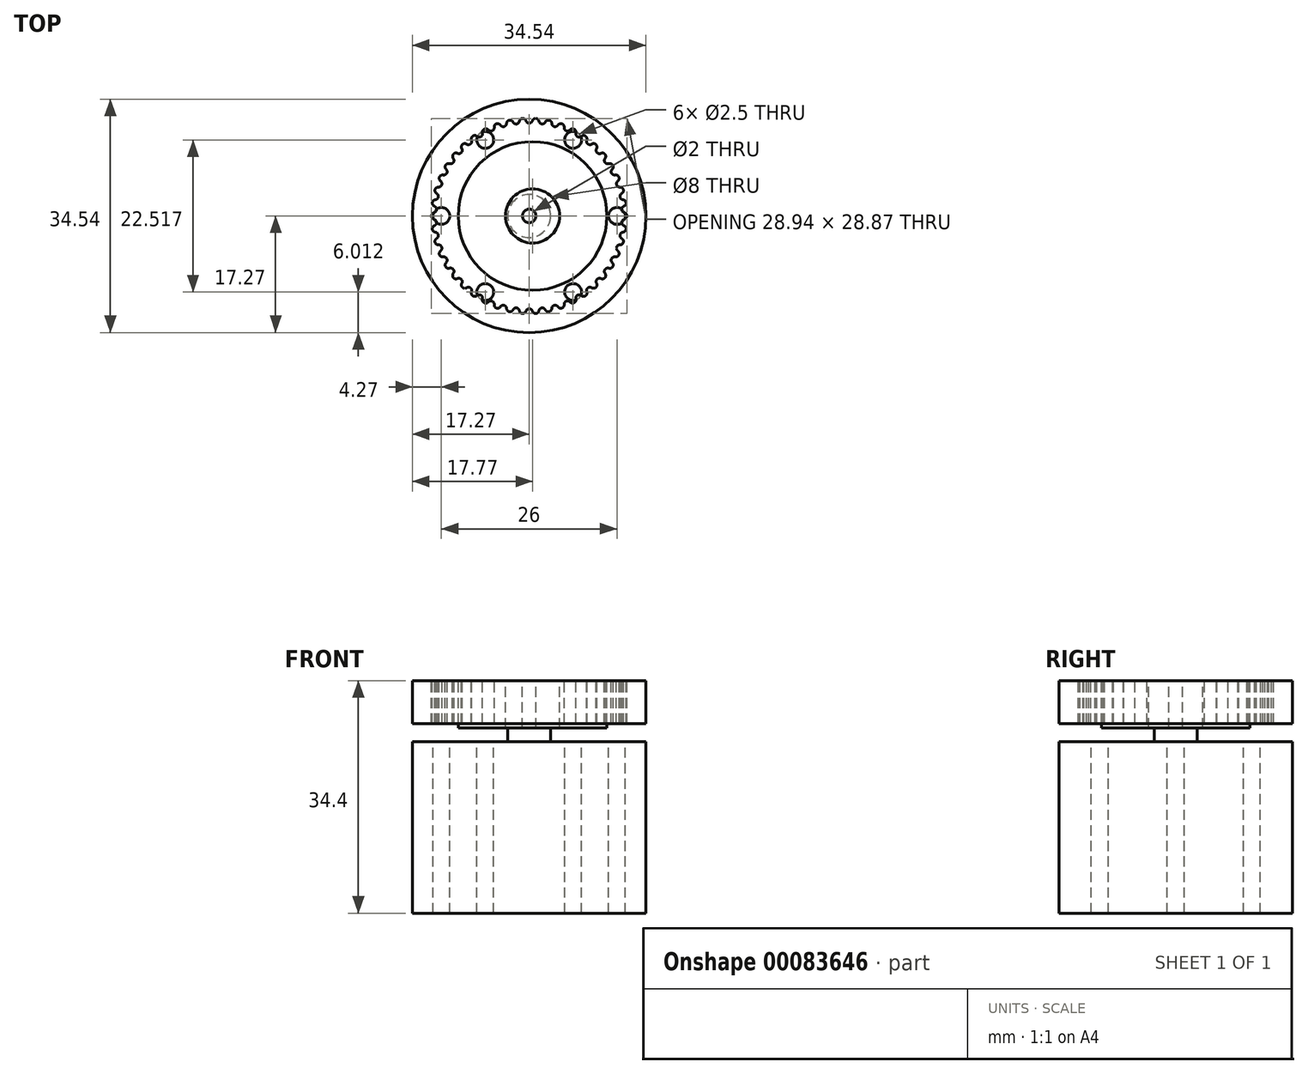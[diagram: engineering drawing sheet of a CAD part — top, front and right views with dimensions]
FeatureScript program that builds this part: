
annotation { "Feature Type Name" : "Feature", "Feature Type Description" : "" }
export const myFeature = defineFeature(function(context is Context, id is Id, definition is map)
    precondition{}
    {
        {
            var Q0;
            Q0=qCreatedBy(makeId("Top.planeOp"),FACE);
            var sketch = newSketch(context, id + "F0", { "sketchPlane" : qUnion([Q0])});
            skCircle(sketch, "E0", {"center": v(0, 0) * mm, "radius": 17.27 * mm});
            skCircle(sketch, "E1", {"center": v(13, 0) * mm, "radius": 1.25 * mm});
            skCircle(sketch, "E2.1.0", {"center": v(6.5, 11.26) * mm, "radius": 1.25 * mm});
            skCircle(sketch, "E2.2.0", {"center": v(-6.5, 11.26) * mm, "radius": 1.25 * mm});
            skCircle(sketch, "E2.3.0", {"center": v(-13, 0) * mm, "radius": 1.25 * mm});
            skCircle(sketch, "E2.4.0", {"center": v(-6.5, -11.26) * mm, "radius": 1.25 * mm});
            skCircle(sketch, "E2.5.0", {"center": v(6.5, -11.26) * mm, "radius": 1.25 * mm});
            skCircle(sketch, "E3", {"center": v(0, 0) * mm, "radius": 1 * mm});
            skCircle(sketch, "E4", {"center": v(0, 0) * mm, "radius": 3.18 * mm});
            skSolve(sketch);
        }
        {
            var Q0;
            Q0 = qSketchRegion(id + "F0", true);
            var Q1;
            Q1=makeQuery(id+"F0.imprint","IMPRINT",FACE,{"disambiguationData":[TD([[makeQuery(id+"F0.imprint","IMPRINT",EDGE,{"derivedFrom":sQuery(id+"F0.wireOp",EDGE,"E3")}),1.0]])]});
            var Q2;
            Q2=makeQuery(id+"F0.imprint","IMPRINT",FACE,{"disambiguationData":[TD([[makeQuery(id+"F0.imprint","IMPRINT",EDGE,{"derivedFrom":sQuery(id+"F0.wireOp",EDGE,"E3")}),-1.0]])]});
            extrude(context, id + "F1", {"entities" : qUnion([Q0, Q1, Q2]), "oppositeDirection" : true, "depth" : 25.4 * mm});
        }
        {
            var Q0;
            Q0=makeQuery(id+"F0.imprint","IMPRINT",FACE,{"disambiguationData":[TD([[makeQuery(id+"F0.imprint","IMPRINT",EDGE,{"derivedFrom":sQuery(id+"F0.wireOp",EDGE,"E3")}),1.0]])]});
            extrude(context, id + "F2", {"entities" : qUnion([Q0]), "operationType" : NewBodyOperationType.ADD, "depth" : 9 * mm});
        }
        {
            var Q0;
            Q0=makeQuery(id+"F0.imprint","IMPRINT",FACE,{"disambiguationData":[TD([[makeQuery(id+"F0.imprint","IMPRINT",EDGE,{"derivedFrom":sQuery(id+"F0.wireOp",EDGE,"E3")}),-1.0]])]});
            extrude(context, id + "F3", {"entities" : qUnion([Q0]), "operationType" : NewBodyOperationType.ADD, "depth" : 2 * mm});
        }
        {
            var Q0;
            Q0=makeQuery(id+"F1.opExtrude","CAP_FACE",FACE,{"disambiguationData":[OSD([sQuery(id+"F0.wireOp",EDGE,"E0"),sQuery(id+"F0.wireOp",EDGE,"E1"),sQuery(id+"F0.wireOp",EDGE,"E2.1.0"),sQuery(id+"F0.wireOp",EDGE,"E2.2.0"),sQuery(id+"F0.wireOp",EDGE,"E2.3.0"),sQuery(id+"F0.wireOp",EDGE,"E2.4.0"),sQuery(id+"F0.wireOp",EDGE,"E2.5.0")])],"isStart":true});
            var sketch = newSketch(context, id + "F4", { "sketchPlane" : qUnion([Q0])});
            skCircle(sketch, "E5.0.0", {"center": v(0, 0) * mm, "radius": 17.27 * mm});
            skCircle(sketch, "E6", {"center": v(0, 0) * mm, "radius": 16 * mm});
            skSolve(sketch);
        }
        {
            var Q0;
            Q0=makeQuery(id+"F2.opExtrude","CAP_FACE",FACE,{"disambiguationData":[OSD([sQuery(id+"F0.wireOp",EDGE,"E3")])],"isStart":false});
            var sketch = newSketch(context, id + "F5", { "sketchPlane" : qUnion([Q0])});
            skCircle(sketch, "E7", {"center": v(0.5, 0) * mm, "radius": 4 * mm});
            skCircle(sketch, "E8", {"center": v(0.5, 0) * mm, "radius": 11 * mm});
            skCircle(sketch, "E9.0", {"center": v(0, 0) * mm, "radius": 1 * mm});
            skArc(sketch, "E10", {"start": v(-14.09, 0.49) * mm, "mid": v(-14.47, 0) * mm, "end": v(-14.09, -0.49) * mm});
            skCircle(sketch, "E11", {"center": v(0, 0) * mm, "radius": 13.97 * mm, "construction": true});
            skArc(sketch, "E12", {"start": v(-14.09, 0.49) * mm, "mid": v(-13.72, 0.87) * mm, "end": v(-13.9, 1.37) * mm});
            skArc(sketch, "E13.MirrorC", {"start": v(-14.09, -0.49) * mm, "mid": v(-14.02, -0.5) * mm, "end": v(-13.96, -0.54) * mm});
            skLineSegment(sketch, "E14", {"start": v(-14.2, 0.97) * mm, "end": v(0, 0) * mm, "construction": true});
            skArc(sketch, "E15.1.0", {"start": v(-14.02, -1.44) * mm, "mid": v(-14.34, -1.97) * mm, "end": v(-13.9, -2.4) * mm});
            skArc(sketch, "E15.1.1", {"start": v(-13.9, -2.4) * mm, "mid": v(-13.82, -2.41) * mm, "end": v(-13.76, -2.43) * mm});
            skArc(sketch, "E15.1.2", {"start": v(-14.02, -1.44) * mm, "mid": v(-13.7, -1) * mm, "end": v(-13.96, -0.54) * mm});
            skArc(sketch, "E15.2.0", {"start": v(-13.7, -3.33) * mm, "mid": v(-13.93, -3.9) * mm, "end": v(-13.43, -4.27) * mm});
            skArc(sketch, "E15.2.1", {"start": v(-13.43, -4.27) * mm, "mid": v(-13.37, -4.27) * mm, "end": v(-13.3, -4.28) * mm});
            skArc(sketch, "E15.2.2", {"start": v(-13.7, -3.33) * mm, "mid": v(-13.44, -2.86) * mm, "end": v(-13.76, -2.43) * mm});
            skArc(sketch, "E15.3.0", {"start": v(-13.12, -5.17) * mm, "mid": v(-13.27, -5.76) * mm, "end": v(-12.73, -6.06) * mm});
            skArc(sketch, "E15.3.1", {"start": v(-12.73, -6.06) * mm, "mid": v(-12.66, -6.05) * mm, "end": v(-12.6, -6.05) * mm});
            skArc(sketch, "E15.3.2", {"start": v(-13.12, -5.17) * mm, "mid": v(-12.93, -4.67) * mm, "end": v(-13.3, -4.28) * mm});
            skArc(sketch, "E15.4.0", {"start": v(-12.29, -6.9) * mm, "mid": v(-12.36, -7.52) * mm, "end": v(-11.78, -7.74) * mm});
            skArc(sketch, "E15.4.1", {"start": v(-11.78, -7.74) * mm, "mid": v(-11.72, -7.72) * mm, "end": v(-11.65, -7.71) * mm});
            skArc(sketch, "E15.4.2", {"start": v(-12.29, -6.9) * mm, "mid": v(-12.17, -6.38) * mm, "end": v(-12.6, -6.05) * mm});
            skArc(sketch, "E15.5.0", {"start": v(-11.23, -8.51) * mm, "mid": v(-11.22, -9.13) * mm, "end": v(-10.62, -9.27) * mm});
            skArc(sketch, "E15.5.1", {"start": v(-10.62, -9.27) * mm, "mid": v(-10.56, -9.24) * mm, "end": v(-10.5, -9.23) * mm});
            skArc(sketch, "E15.5.2", {"start": v(-11.23, -8.51) * mm, "mid": v(-11.19, -7.98) * mm, "end": v(-11.65, -7.71) * mm});
            skArc(sketch, "E15.6.0", {"start": v(-9.97, -9.96) * mm, "mid": v(-9.88, -10.58) * mm, "end": v(-9.26, -10.63) * mm});
            skArc(sketch, "E15.6.1", {"start": v(-9.26, -10.63) * mm, "mid": v(-9.2, -10.6) * mm, "end": v(-9.14, -10.57) * mm});
            skArc(sketch, "E15.6.2", {"start": v(-9.97, -9.96) * mm, "mid": v(-10, -9.43) * mm, "end": v(-10.5, -9.23) * mm});
            skArc(sketch, "E15.7.0", {"start": v(-8.52, -11.23) * mm, "mid": v(-8.34, -11.82) * mm, "end": v(-7.73, -11.79) * mm});
            skArc(sketch, "E15.7.1", {"start": v(-7.73, -11.79) * mm, "mid": v(-7.67, -11.75) * mm, "end": v(-7.61, -11.71) * mm});
            skArc(sketch, "E15.7.2", {"start": v(-8.52, -11.23) * mm, "mid": v(-8.62, -10.7) * mm, "end": v(-9.14, -10.57) * mm});
            skArc(sketch, "E15.8.0", {"start": v(-6.91, -12.29) * mm, "mid": v(-6.66, -12.85) * mm, "end": v(-6.05, -12.73) * mm});
            skArc(sketch, "E15.8.1", {"start": v(-6.05, -12.73) * mm, "mid": v(-6, -12.68) * mm, "end": v(-5.95, -12.64) * mm});
            skArc(sketch, "E15.8.2", {"start": v(-6.91, -12.29) * mm, "mid": v(-7.08, -11.78) * mm, "end": v(-7.61, -11.71) * mm});
            skArc(sketch, "E15.9.0", {"start": v(-5.18, -13.11) * mm, "mid": v(-4.85, -13.63) * mm, "end": v(-4.26, -13.44) * mm});
            skArc(sketch, "E15.9.1", {"start": v(-4.26, -13.44) * mm, "mid": v(-4.22, -13.38) * mm, "end": v(-4.17, -13.33) * mm});
            skArc(sketch, "E15.9.2", {"start": v(-5.18, -13.11) * mm, "mid": v(-5.41, -12.63) * mm, "end": v(-5.95, -12.64) * mm});
            skArc(sketch, "E15.10.0", {"start": v(-3.34, -13.7) * mm, "mid": v(-2.94, -14.17) * mm, "end": v(-2.4, -13.9) * mm});
            skArc(sketch, "E15.10.1", {"start": v(-2.4, -13.9) * mm, "mid": v(-2.36, -13.83) * mm, "end": v(-2.31, -13.78) * mm});
            skArc(sketch, "E15.10.2", {"start": v(-3.34, -13.7) * mm, "mid": v(-3.64, -13.25) * mm, "end": v(-4.17, -13.33) * mm});
            skArc(sketch, "E15.11.0", {"start": v(-1.45, -14.02) * mm, "mid": v(-0.99, -14.44) * mm, "end": v(-0.48, -14.09) * mm});
            skArc(sketch, "E15.11.1", {"start": v(-0.48, -14.09) * mm, "mid": v(-0.45, -14.02) * mm, "end": v(-0.42, -13.96) * mm});
            skArc(sketch, "E15.11.2", {"start": v(-1.45, -14.02) * mm, "mid": v(-1.8, -13.63) * mm, "end": v(-2.31, -13.78) * mm});
            skArc(sketch, "E15.12.0", {"start": v(0.48, -14.09) * mm, "mid": v(0.99, -14.44) * mm, "end": v(1.45, -14.02) * mm});
            skArc(sketch, "E15.12.1", {"start": v(1.45, -14.02) * mm, "mid": v(1.46, -13.95) * mm, "end": v(1.49, -13.9) * mm});
            skArc(sketch, "E15.12.2", {"start": v(0.48, -14.09) * mm, "mid": v(0.07, -13.74) * mm, "end": v(-0.42, -13.96) * mm});
            skArc(sketch, "E15.13.0", {"start": v(2.4, -13.9) * mm, "mid": v(2.94, -14.17) * mm, "end": v(3.34, -13.7) * mm});
            skArc(sketch, "E15.13.1", {"start": v(3.34, -13.7) * mm, "mid": v(3.35, -13.63) * mm, "end": v(3.37, -13.56) * mm});
            skArc(sketch, "E15.13.2", {"start": v(2.4, -13.9) * mm, "mid": v(1.94, -13.6) * mm, "end": v(1.49, -13.9) * mm});
            skArc(sketch, "E15.14.0", {"start": v(4.26, -13.44) * mm, "mid": v(4.85, -13.63) * mm, "end": v(5.18, -13.11) * mm});
            skArc(sketch, "E15.14.1", {"start": v(5.18, -13.11) * mm, "mid": v(5.17, -13.04) * mm, "end": v(5.18, -12.97) * mm});
            skArc(sketch, "E15.14.2", {"start": v(4.26, -13.44) * mm, "mid": v(3.77, -13.22) * mm, "end": v(3.37, -13.56) * mm});
            skArc(sketch, "E15.15.0", {"start": v(6.05, -12.73) * mm, "mid": v(6.66, -12.85) * mm, "end": v(6.91, -12.29) * mm});
            skArc(sketch, "E15.15.1", {"start": v(6.91, -12.29) * mm, "mid": v(6.9, -12.22) * mm, "end": v(6.9, -12.15) * mm});
            skArc(sketch, "E15.15.2", {"start": v(6.05, -12.73) * mm, "mid": v(5.54, -12.58) * mm, "end": v(5.18, -12.97) * mm});
            skArc(sketch, "E15.16.0", {"start": v(7.73, -11.79) * mm, "mid": v(8.34, -11.82) * mm, "end": v(8.52, -11.23) * mm});
            skArc(sketch, "E15.16.1", {"start": v(8.52, -11.23) * mm, "mid": v(8.5, -11.16) * mm, "end": v(8.49, -11.1) * mm});
            skArc(sketch, "E15.16.2", {"start": v(7.73, -11.79) * mm, "mid": v(7.2, -11.7) * mm, "end": v(6.9, -12.15) * mm});
            skArc(sketch, "E15.17.0", {"start": v(9.26, -10.63) * mm, "mid": v(9.88, -10.58) * mm, "end": v(9.97, -9.96) * mm});
            skArc(sketch, "E15.17.1", {"start": v(9.97, -9.96) * mm, "mid": v(9.94, -9.9) * mm, "end": v(9.92, -9.84) * mm});
            skArc(sketch, "E15.17.2", {"start": v(9.26, -10.63) * mm, "mid": v(8.73, -10.62) * mm, "end": v(8.49, -11.1) * mm});
            skArc(sketch, "E15.18.0", {"start": v(10.62, -9.27) * mm, "mid": v(11.22, -9.13) * mm, "end": v(11.23, -8.51) * mm});
            skArc(sketch, "E15.18.1", {"start": v(11.23, -8.51) * mm, "mid": v(11.2, -8.46) * mm, "end": v(11.17, -8.4) * mm});
            skArc(sketch, "E15.18.2", {"start": v(10.62, -9.27) * mm, "mid": v(10.1, -9.33) * mm, "end": v(9.92, -9.84) * mm});
            skArc(sketch, "E15.19.0", {"start": v(11.78, -7.74) * mm, "mid": v(12.36, -7.52) * mm, "end": v(12.29, -6.9) * mm});
            skArc(sketch, "E15.19.1", {"start": v(12.29, -6.9) * mm, "mid": v(12.24, -6.85) * mm, "end": v(12.2, -6.8) * mm});
            skArc(sketch, "E15.19.2", {"start": v(11.78, -7.74) * mm, "mid": v(11.27, -7.87) * mm, "end": v(11.17, -8.4) * mm});
            skArc(sketch, "E15.20.0", {"start": v(12.73, -6.06) * mm, "mid": v(13.27, -5.76) * mm, "end": v(13.12, -5.17) * mm});
            skArc(sketch, "E15.20.1", {"start": v(13.12, -5.17) * mm, "mid": v(13.06, -5.12) * mm, "end": v(13.02, -5.07) * mm});
            skArc(sketch, "E15.20.2", {"start": v(12.73, -6.06) * mm, "mid": v(12.23, -6.26) * mm, "end": v(12.2, -6.8) * mm});
            skArc(sketch, "E15.21.0", {"start": v(13.43, -4.27) * mm, "mid": v(13.93, -3.9) * mm, "end": v(13.7, -3.33) * mm});
            skArc(sketch, "E15.21.1", {"start": v(13.7, -3.33) * mm, "mid": v(13.64, -3.3) * mm, "end": v(13.59, -3.25) * mm});
            skArc(sketch, "E15.21.2", {"start": v(13.43, -4.27) * mm, "mid": v(12.97, -4.54) * mm, "end": v(13.02, -5.07) * mm});
            skArc(sketch, "E15.22.0", {"start": v(13.9, -2.4) * mm, "mid": v(14.34, -1.97) * mm, "end": v(14.02, -1.44) * mm});
            skArc(sketch, "E15.22.1", {"start": v(14.02, -1.44) * mm, "mid": v(13.96, -1.4) * mm, "end": v(13.9, -1.37) * mm});
            skArc(sketch, "E15.22.2", {"start": v(13.9, -2.4) * mm, "mid": v(13.47, -2.73) * mm, "end": v(13.59, -3.25) * mm});
            skArc(sketch, "E15.23.0", {"start": v(14.09, -0.49) * mm, "mid": v(14.47, 0) * mm, "end": v(14.09, 0.49) * mm});
            skArc(sketch, "E15.23.1", {"start": v(14.09, 0.49) * mm, "mid": v(14.02, 0.5) * mm, "end": v(13.96, 0.54) * mm});
            skArc(sketch, "E15.23.2", {"start": v(14.09, -0.49) * mm, "mid": v(13.72, -0.87) * mm, "end": v(13.9, -1.37) * mm});
            skArc(sketch, "E15.24.0", {"start": v(14.02, 1.44) * mm, "mid": v(14.34, 1.97) * mm, "end": v(13.9, 2.4) * mm});
            skArc(sketch, "E15.24.1", {"start": v(13.9, 2.4) * mm, "mid": v(13.82, 2.41) * mm, "end": v(13.76, 2.43) * mm});
            skArc(sketch, "E15.24.2", {"start": v(14.02, 1.44) * mm, "mid": v(13.7, 1) * mm, "end": v(13.96, 0.54) * mm});
            skArc(sketch, "E15.25.0", {"start": v(13.7, 3.33) * mm, "mid": v(13.93, 3.9) * mm, "end": v(13.43, 4.27) * mm});
            skArc(sketch, "E15.25.1", {"start": v(13.43, 4.27) * mm, "mid": v(13.37, 4.27) * mm, "end": v(13.3, 4.28) * mm});
            skArc(sketch, "E15.25.2", {"start": v(13.7, 3.33) * mm, "mid": v(13.44, 2.86) * mm, "end": v(13.76, 2.43) * mm});
            skArc(sketch, "E15.26.0", {"start": v(13.12, 5.17) * mm, "mid": v(13.27, 5.76) * mm, "end": v(12.73, 6.06) * mm});
            skArc(sketch, "E15.26.1", {"start": v(12.73, 6.06) * mm, "mid": v(12.66, 6.05) * mm, "end": v(12.6, 6.05) * mm});
            skArc(sketch, "E15.26.2", {"start": v(13.12, 5.17) * mm, "mid": v(12.93, 4.67) * mm, "end": v(13.3, 4.28) * mm});
            skArc(sketch, "E15.27.0", {"start": v(12.29, 6.9) * mm, "mid": v(12.36, 7.52) * mm, "end": v(11.78, 7.74) * mm});
            skArc(sketch, "E15.27.1", {"start": v(11.78, 7.74) * mm, "mid": v(11.72, 7.72) * mm, "end": v(11.65, 7.71) * mm});
            skArc(sketch, "E15.27.2", {"start": v(12.29, 6.9) * mm, "mid": v(12.17, 6.38) * mm, "end": v(12.6, 6.05) * mm});
            skArc(sketch, "E15.28.0", {"start": v(11.23, 8.51) * mm, "mid": v(11.22, 9.13) * mm, "end": v(10.62, 9.27) * mm});
            skArc(sketch, "E15.28.1", {"start": v(10.62, 9.27) * mm, "mid": v(10.56, 9.24) * mm, "end": v(10.5, 9.23) * mm});
            skArc(sketch, "E15.28.2", {"start": v(11.23, 8.51) * mm, "mid": v(11.19, 7.98) * mm, "end": v(11.65, 7.71) * mm});
            skArc(sketch, "E15.29.0", {"start": v(9.97, 9.96) * mm, "mid": v(9.88, 10.58) * mm, "end": v(9.26, 10.63) * mm});
            skArc(sketch, "E15.29.1", {"start": v(9.26, 10.63) * mm, "mid": v(9.2, 10.6) * mm, "end": v(9.14, 10.57) * mm});
            skArc(sketch, "E15.29.2", {"start": v(9.97, 9.96) * mm, "mid": v(10, 9.43) * mm, "end": v(10.5, 9.23) * mm});
            skArc(sketch, "E15.30.0", {"start": v(8.52, 11.23) * mm, "mid": v(8.34, 11.82) * mm, "end": v(7.73, 11.79) * mm});
            skArc(sketch, "E15.30.1", {"start": v(7.73, 11.79) * mm, "mid": v(7.67, 11.75) * mm, "end": v(7.61, 11.71) * mm});
            skArc(sketch, "E15.30.2", {"start": v(8.52, 11.23) * mm, "mid": v(8.62, 10.7) * mm, "end": v(9.14, 10.57) * mm});
            skArc(sketch, "E15.31.0", {"start": v(6.91, 12.29) * mm, "mid": v(6.66, 12.85) * mm, "end": v(6.05, 12.73) * mm});
            skArc(sketch, "E15.31.1", {"start": v(6.05, 12.73) * mm, "mid": v(6, 12.68) * mm, "end": v(5.95, 12.64) * mm});
            skArc(sketch, "E15.31.2", {"start": v(6.91, 12.29) * mm, "mid": v(7.08, 11.78) * mm, "end": v(7.61, 11.71) * mm});
            skArc(sketch, "E15.32.0", {"start": v(5.18, 13.11) * mm, "mid": v(4.85, 13.63) * mm, "end": v(4.26, 13.44) * mm});
            skArc(sketch, "E15.32.1", {"start": v(4.26, 13.44) * mm, "mid": v(4.22, 13.38) * mm, "end": v(4.17, 13.33) * mm});
            skArc(sketch, "E15.32.2", {"start": v(5.18, 13.11) * mm, "mid": v(5.41, 12.63) * mm, "end": v(5.95, 12.64) * mm});
            skArc(sketch, "E15.33.0", {"start": v(3.34, 13.7) * mm, "mid": v(2.94, 14.17) * mm, "end": v(2.4, 13.9) * mm});
            skArc(sketch, "E15.33.1", {"start": v(2.4, 13.9) * mm, "mid": v(2.36, 13.83) * mm, "end": v(2.31, 13.78) * mm});
            skArc(sketch, "E15.33.2", {"start": v(3.34, 13.7) * mm, "mid": v(3.64, 13.25) * mm, "end": v(4.17, 13.33) * mm});
            skArc(sketch, "E15.34.0", {"start": v(1.45, 14.02) * mm, "mid": v(0.99, 14.44) * mm, "end": v(0.48, 14.09) * mm});
            skArc(sketch, "E15.34.1", {"start": v(0.48, 14.09) * mm, "mid": v(0.45, 14.02) * mm, "end": v(0.42, 13.96) * mm});
            skArc(sketch, "E15.34.2", {"start": v(1.45, 14.02) * mm, "mid": v(1.8, 13.63) * mm, "end": v(2.31, 13.78) * mm});
            skArc(sketch, "E15.35.0", {"start": v(-0.48, 14.09) * mm, "mid": v(-0.99, 14.44) * mm, "end": v(-1.45, 14.02) * mm});
            skArc(sketch, "E15.35.1", {"start": v(-1.45, 14.02) * mm, "mid": v(-1.46, 13.95) * mm, "end": v(-1.49, 13.9) * mm});
            skArc(sketch, "E15.35.2", {"start": v(-0.48, 14.09) * mm, "mid": v(-0.07, 13.74) * mm, "end": v(0.42, 13.96) * mm});
            skArc(sketch, "E15.36.0", {"start": v(-2.4, 13.9) * mm, "mid": v(-2.94, 14.17) * mm, "end": v(-3.34, 13.7) * mm});
            skArc(sketch, "E15.36.1", {"start": v(-3.34, 13.7) * mm, "mid": v(-3.35, 13.63) * mm, "end": v(-3.37, 13.56) * mm});
            skArc(sketch, "E15.36.2", {"start": v(-2.4, 13.9) * mm, "mid": v(-1.94, 13.6) * mm, "end": v(-1.49, 13.9) * mm});
            skArc(sketch, "E15.37.0", {"start": v(-4.26, 13.44) * mm, "mid": v(-4.85, 13.63) * mm, "end": v(-5.18, 13.11) * mm});
            skArc(sketch, "E15.37.1", {"start": v(-5.18, 13.11) * mm, "mid": v(-5.17, 13.04) * mm, "end": v(-5.18, 12.97) * mm});
            skArc(sketch, "E15.37.2", {"start": v(-4.26, 13.44) * mm, "mid": v(-3.77, 13.22) * mm, "end": v(-3.37, 13.56) * mm});
            skArc(sketch, "E15.38.0", {"start": v(-6.05, 12.73) * mm, "mid": v(-6.66, 12.85) * mm, "end": v(-6.91, 12.29) * mm});
            skArc(sketch, "E15.38.1", {"start": v(-6.91, 12.29) * mm, "mid": v(-6.9, 12.22) * mm, "end": v(-6.9, 12.15) * mm});
            skArc(sketch, "E15.38.2", {"start": v(-6.05, 12.73) * mm, "mid": v(-5.54, 12.58) * mm, "end": v(-5.18, 12.97) * mm});
            skArc(sketch, "E15.39.0", {"start": v(-7.73, 11.79) * mm, "mid": v(-8.34, 11.82) * mm, "end": v(-8.52, 11.23) * mm});
            skArc(sketch, "E15.39.1", {"start": v(-8.52, 11.23) * mm, "mid": v(-8.5, 11.16) * mm, "end": v(-8.49, 11.1) * mm});
            skArc(sketch, "E15.39.2", {"start": v(-7.73, 11.79) * mm, "mid": v(-7.2, 11.7) * mm, "end": v(-6.9, 12.15) * mm});
            skArc(sketch, "E15.40.0", {"start": v(-9.26, 10.63) * mm, "mid": v(-9.88, 10.58) * mm, "end": v(-9.97, 9.96) * mm});
            skArc(sketch, "E15.40.1", {"start": v(-9.97, 9.96) * mm, "mid": v(-9.94, 9.9) * mm, "end": v(-9.92, 9.84) * mm});
            skArc(sketch, "E15.40.2", {"start": v(-9.26, 10.63) * mm, "mid": v(-8.73, 10.62) * mm, "end": v(-8.49, 11.1) * mm});
            skArc(sketch, "E15.41.0", {"start": v(-10.62, 9.27) * mm, "mid": v(-11.22, 9.13) * mm, "end": v(-11.23, 8.51) * mm});
            skArc(sketch, "E15.41.1", {"start": v(-11.23, 8.51) * mm, "mid": v(-11.2, 8.46) * mm, "end": v(-11.17, 8.4) * mm});
            skArc(sketch, "E15.41.2", {"start": v(-10.62, 9.27) * mm, "mid": v(-10.1, 9.33) * mm, "end": v(-9.92, 9.84) * mm});
            skArc(sketch, "E15.42.0", {"start": v(-11.78, 7.74) * mm, "mid": v(-12.36, 7.52) * mm, "end": v(-12.29, 6.9) * mm});
            skArc(sketch, "E15.42.1", {"start": v(-12.29, 6.9) * mm, "mid": v(-12.24, 6.85) * mm, "end": v(-12.2, 6.8) * mm});
            skArc(sketch, "E15.42.2", {"start": v(-11.78, 7.74) * mm, "mid": v(-11.27, 7.87) * mm, "end": v(-11.17, 8.4) * mm});
            skArc(sketch, "E15.43.0", {"start": v(-12.73, 6.06) * mm, "mid": v(-13.27, 5.76) * mm, "end": v(-13.12, 5.17) * mm});
            skArc(sketch, "E15.43.1", {"start": v(-13.12, 5.17) * mm, "mid": v(-13.06, 5.12) * mm, "end": v(-13.02, 5.07) * mm});
            skArc(sketch, "E15.43.2", {"start": v(-12.73, 6.06) * mm, "mid": v(-12.23, 6.26) * mm, "end": v(-12.2, 6.8) * mm});
            skArc(sketch, "E15.44.0", {"start": v(-13.43, 4.27) * mm, "mid": v(-13.93, 3.9) * mm, "end": v(-13.7, 3.33) * mm});
            skArc(sketch, "E15.44.1", {"start": v(-13.7, 3.33) * mm, "mid": v(-13.64, 3.3) * mm, "end": v(-13.59, 3.25) * mm});
            skArc(sketch, "E15.44.2", {"start": v(-13.43, 4.27) * mm, "mid": v(-12.97, 4.54) * mm, "end": v(-13.02, 5.07) * mm});
            skArc(sketch, "E15.45.0", {"start": v(-13.9, 2.4) * mm, "mid": v(-14.34, 1.97) * mm, "end": v(-14.02, 1.44) * mm});
            skArc(sketch, "E15.45.1", {"start": v(-14.02, 1.44) * mm, "mid": v(-13.96, 1.4) * mm, "end": v(-13.9, 1.37) * mm});
            skArc(sketch, "E15.45.2", {"start": v(-13.9, 2.4) * mm, "mid": v(-13.47, 2.73) * mm, "end": v(-13.59, 3.25) * mm});
            skCircle(sketch, "E16.0", {"center": v(0, 0) * mm, "radius": 17.27 * mm});
            skSolve(sketch);
        }
        {
            var Q0;
            Q0=makeQuery(id+"F5.imprint","IMPRINT",FACE,{"disambiguationData":[TD([[makeQuery(id+"F5.imprint","IMPRINT",EDGE,{"derivedFrom":sQuery(id+"F5.wireOp",EDGE,"E7")}),1.0]])]});
            extrude(context, id + "F6", {"entities" : qUnion([Q0]), "oppositeDirection" : true, "depth" : 7 * mm});
        }
        {
            var Q0;
            Q0=makeQuery(id+"F5.imprint","IMPRINT",FACE,{"disambiguationData":[TD([[makeQuery(id+"F5.imprint","IMPRINT",EDGE,{"derivedFrom":sQuery(id+"F5.wireOp",EDGE,"E7")}),-1.0]])]});
            extrude(context, id + "F7", {"entities" : qUnion([Q0]), "oppositeDirection" : true, "depth" : 7 * mm});
        }
        {
            var Q0;
            Q0 = qSketchRegion(id + "F5", true);
            extrude(context, id + "F8", {"entities" : qUnion([Q0]), "oppositeDirection" : true, "depth" : 6.35 * mm});
        }
    });
